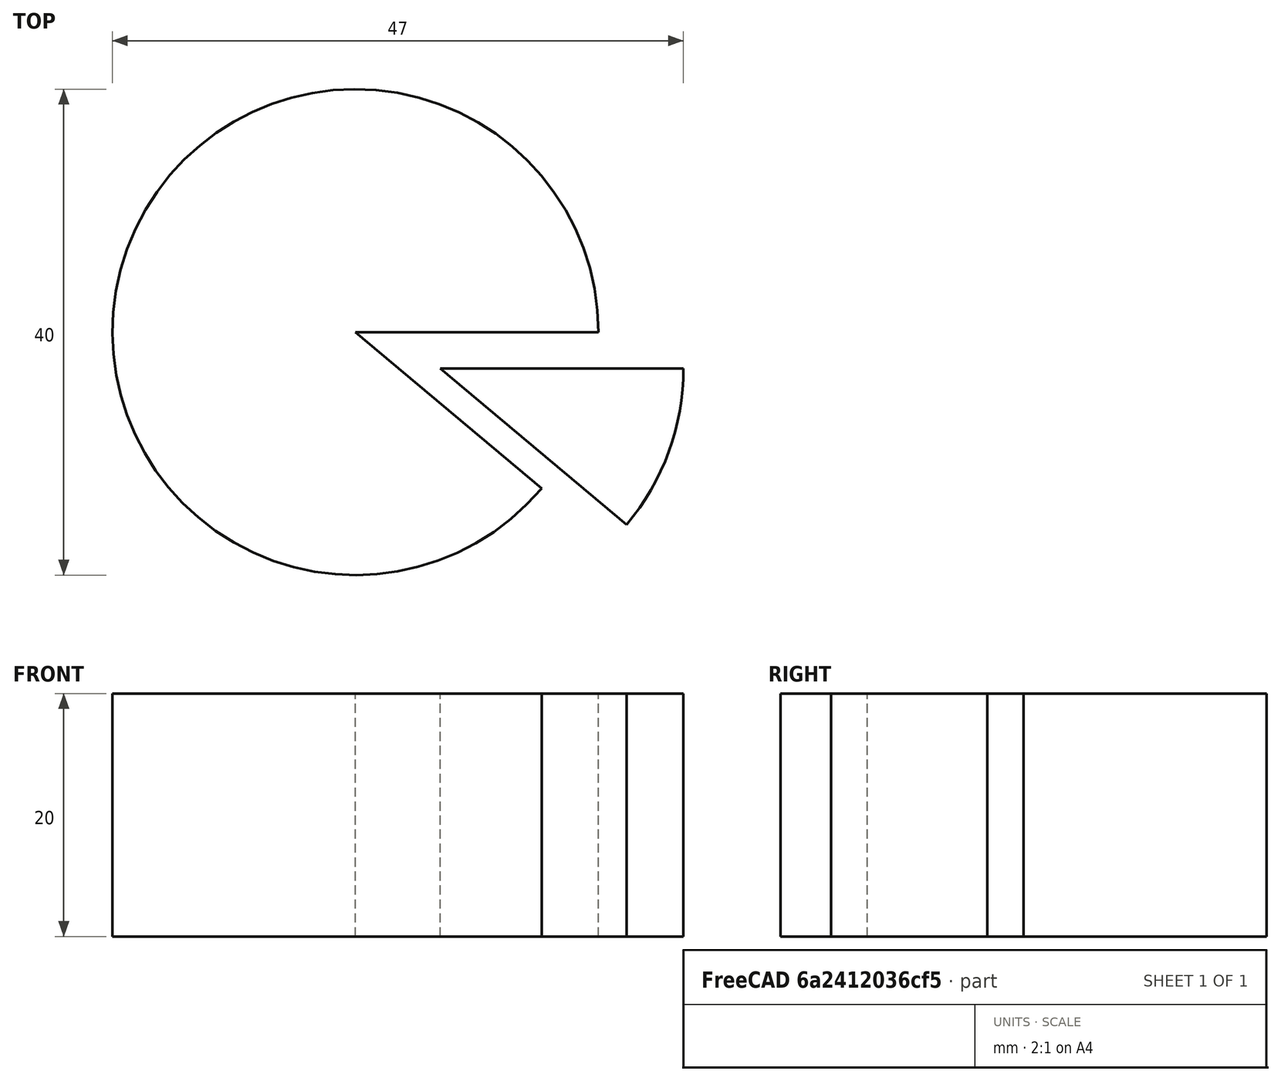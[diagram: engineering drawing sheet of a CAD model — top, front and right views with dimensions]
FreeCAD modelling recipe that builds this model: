
FCSTD DOCUMENT  (FreeCAD 0.20R29177 (Git))
Label: Ejercicio1Video9
License: All rights reserved
LicenseURL: http://en.wikipedia.org/wiki/All_rights_reserved
objects: Part::Cylinder×3, Part::Cut×1
note: 4 computed .brp shape members not serialized (recipe doc carries the construction recipe); baked Part::Feature solids carry a one-line shape summary decoded from their .brp

FEATURE [Part::Cylinder] Cylinder  label="tarta"
  Angle = 320
  AttacherType = Attacher::AttachEngine3D
  FirstAngle = 0
  Height = 20
  Radius = 20
  SecondAngle = 0
FEATURE [Part::Cylinder] Cylinder001  label="tarta001"
  Angle = 320
  AttacherType = Attacher::AttachEngine3D
  FirstAngle = 0
  Height = 20
  Placement = pos=(7,-3,0) rot=(0,0,1;0rad)
  Radius = 20
  SecondAngle = 0
FEATURE [Part::Cylinder] Cylinder002  label="tarta002"
  Angle = 360
  AttacherType = Attacher::AttachEngine3D
  FirstAngle = 0
  Height = 20
  Placement = pos=(7,-3,0) rot=(0,0,1;0rad)
  Radius = 20
  SecondAngle = 0
FEATURE [Part::Cut] Cut  label="trozo"
  Base = -> Cylinder002
  Tool = -> Cylinder001
